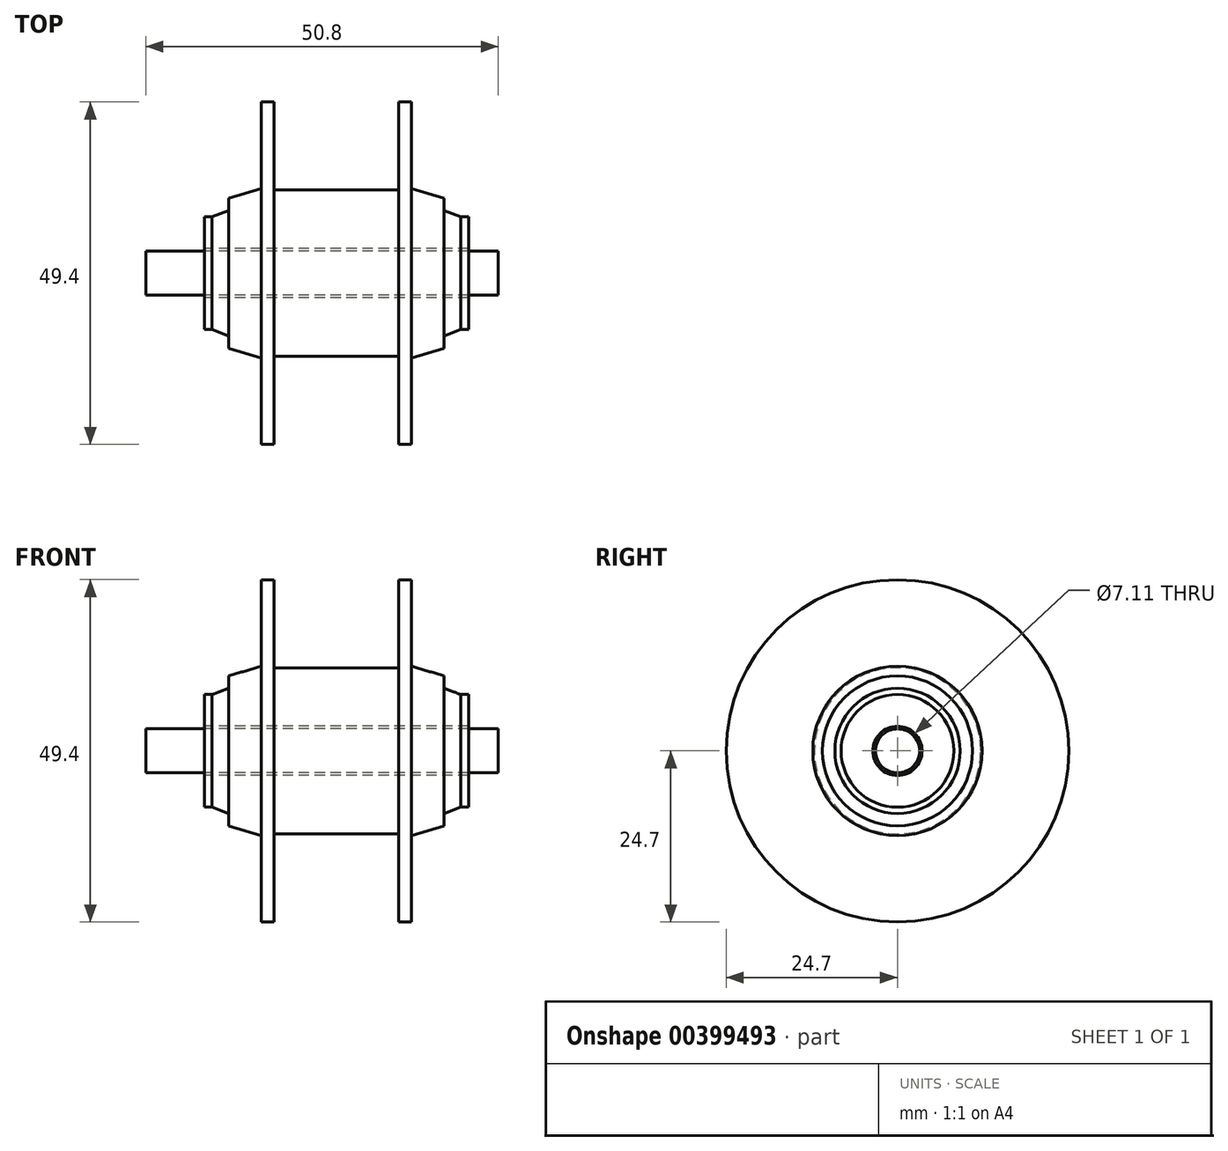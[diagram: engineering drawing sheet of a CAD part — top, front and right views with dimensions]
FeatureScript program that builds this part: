
annotation { "Feature Type Name" : "Feature", "Feature Type Description" : "" }
export const myFeature = defineFeature(function(context is Context, id is Id, definition is map)
    precondition{}
    {
        {
            var Q0;
            Q0=qCreatedBy(makeId("Right.planeOp"),FACE);
            var sketch = newSketch(context, id + "F0", { "sketchPlane" : qUnion([Q0])});
            skCircle(sketch, "E0", {"center": v(0, 0) * mm, "radius": 3.18 * mm});
            skSolve(sketch);
        }
        {
            var Q0;
            Q0 = qSketchRegion(id + "F0", true);
            extrude(context, id + "F1", {"entities" : qUnion([Q0]), "depth" : 50.8 * mm});
        }
        {
            var Q0;
            Q0=qCreatedBy(makeId("Front.planeOp"),FACE);
            var sketch = newSketch(context, id + "F2", { "sketchPlane" : qUnion([Q0])});
            skLineSegment(sketch, "E1.bottom", {"start": v(8.42, 0) * mm, "end": v(46.52, 0) * mm});
            skLineSegment(sketch, "E1.top", {"start": v(8.42, 3.56) * mm, "end": v(46.52, 3.56) * mm});
            skLineSegment(sketch, "E1.left", {"start": v(8.42, 0) * mm, "end": v(8.42, 3.56) * mm});
            skLineSegment(sketch, "E1.right", {"start": v(46.52, 0) * mm, "end": v(46.52, 3.56) * mm});
            skLineSegment(sketch, "E2", {"start": v(36.46, 12) * mm, "end": v(36.46, 24.7) * mm});
            skLineSegment(sketch, "E3", {"start": v(36.46, 24.7) * mm, "end": v(38.31, 24.7) * mm});
            skLineSegment(sketch, "E4", {"start": v(38.31, 24.7) * mm, "end": v(38.31, 12.84) * mm});
            skLineSegment(sketch, "E5", {"start": v(38.31, 12.84) * mm, "end": v(38.31, 12.2) * mm});
            skLineSegment(sketch, "E6", {"start": v(38.31, 12.2) * mm, "end": v(43, 10.82) * mm});
            skLineSegment(sketch, "E7", {"start": v(43, 10.82) * mm, "end": v(43, 9.03) * mm});
            skLineSegment(sketch, "E8", {"start": v(43, 9.03) * mm, "end": v(45.4, 8.13) * mm});
            skLineSegment(sketch, "E9", {"start": v(45.4, 8.13) * mm, "end": v(46.52, 8.13) * mm});
            skLineSegment(sketch, "E10", {"start": v(46.52, 8.13) * mm, "end": v(46.52, 3.56) * mm});
            skLineSegment(sketch, "E11.MirrorCS", {"start": v(8.42, 8.13) * mm, "end": v(8.42, 3.56) * mm});
            skLineSegment(sketch, "E12.MirrorCS", {"start": v(18.48, 24.7) * mm, "end": v(16.63, 24.7) * mm});
            skLineSegment(sketch, "E13.MirrorCS", {"start": v(11.94, 10.82) * mm, "end": v(11.94, 9.03) * mm});
            skLineSegment(sketch, "E14.MirrorCS", {"start": v(11.94, 9.03) * mm, "end": v(9.54, 8.13) * mm});
            skLineSegment(sketch, "E15.MirrorCS", {"start": v(9.54, 8.13) * mm, "end": v(8.42, 8.13) * mm});
            skLineSegment(sketch, "E16.MirrorCS", {"start": v(18.48, 12) * mm, "end": v(18.48, 24.7) * mm});
            skLineSegment(sketch, "E17.MirrorCS", {"start": v(36.46, 12) * mm, "end": v(18.48, 12) * mm});
            skLineSegment(sketch, "E18.MirrorCS", {"start": v(16.63, 19.54) * mm, "end": v(16.63, 12.2) * mm});
            skLineSegment(sketch, "E19.MirrorCS", {"start": v(16.63, 12.2) * mm, "end": v(11.94, 10.82) * mm});
            skLineSegment(sketch, "E20.MirrorCS", {"start": v(16.63, 24.7) * mm, "end": v(16.63, 19.54) * mm});
            skSolve(sketch);
        }
        {
            var Q0;
            Q0=makeQuery(id+"F2.imprint","IMPRINT",FACE,{"disambiguationData":[TD([[makeQuery(id+"F2.imprint","IMPRINT",EDGE,{"derivedFrom":sQuery(id+"F2.wireOp",EDGE,"E1.top")}),1.0]])]});
            var Q1;
            Q1=sQuery(id+"F2.wireOp",EDGE,"E1.bottom");
            revolve(context, id + "F3", {"entities" : qUnion([Q0]), "axis" : qUnion([Q1]), "revolveType" : RevolveType.FULL});
        }
    });
